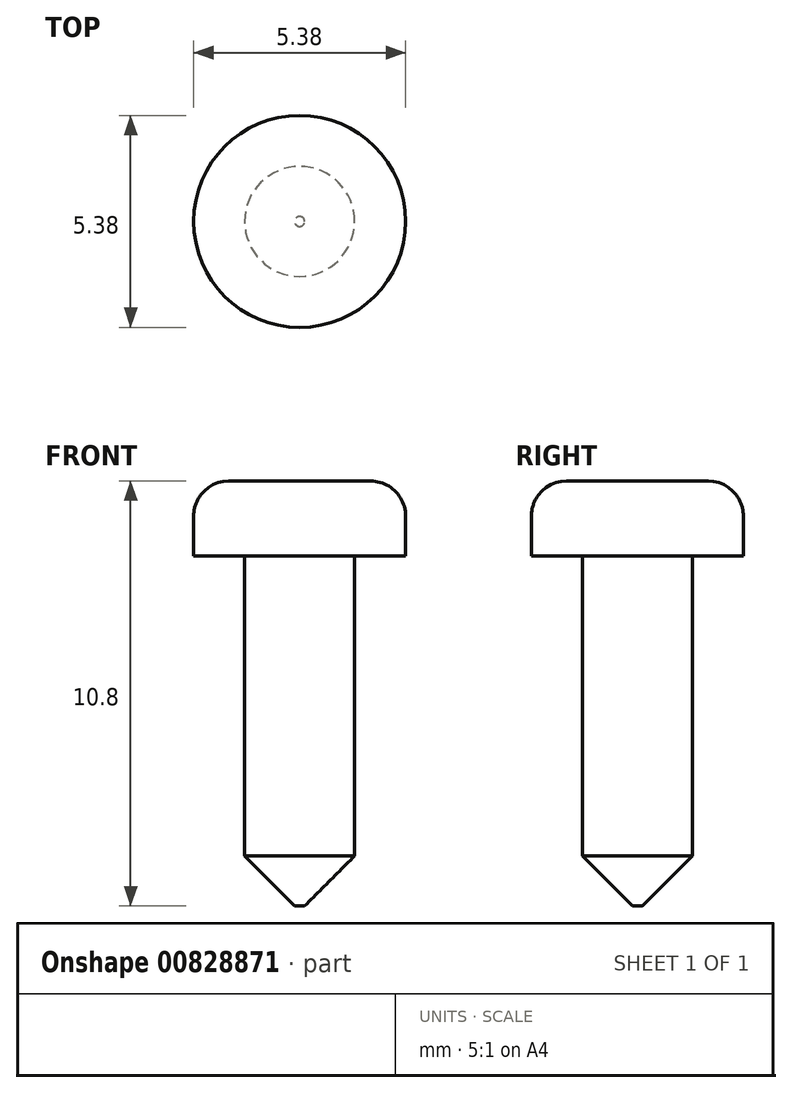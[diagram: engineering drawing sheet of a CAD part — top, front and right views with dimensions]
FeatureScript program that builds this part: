
annotation { "Feature Type Name" : "Feature", "Feature Type Description" : "" }
export const myFeature = defineFeature(function(context is Context, id is Id, definition is map)
    precondition{}
    {
        {
            var Q0;
            Q0=qCreatedBy(makeId("Top.planeOp"),FACE);
            var sketch = newSketch(context, id + "F0", { "sketchPlane" : qUnion([Q0])});
            skCircle(sketch, "E0", {"center": v(0, 0) * mm, "radius": 2.7 * mm});
            skSolve(sketch);
        }
        {
            var Q0;
            Q0 = qSketchRegion(id + "F0", true);
            extrude(context, id + "F1", {"entities" : qUnion([Q0]), "depth" : 1.9 * mm, "offsetDistance" : 25.4 * mm});
        }
        {
            var Q0;
            Q0=makeQuery(id+"F1.opExtrude","CAP_EDGE",EDGE,{"disambiguationData":[OSD([sQuery(id+"F0.wireOp",EDGE,"E0")])],"isStart":false});
            fillet(context, id + "F2", {"entities" : qUnion([Q0]), "radius" : 0.89 * mm, "tangentPropagation" : true, "allowEdgeOverflow" : false});
        }
        {
            var Q0;
            Q0=qCreatedBy(makeId("Top.planeOp"),FACE);
            var sketch = newSketch(context, id + "F3", { "sketchPlane" : qUnion([Q0])});
            skCircle(sketch, "E1", {"center": v(0, 0) * mm, "radius": 1.4 * mm});
            skSolve(sketch);
        }
        {
            var Q0;
            Q0 = qSketchRegion(id + "F3", true);
            extrude(context, id + "F4", {"entities" : qUnion([Q0]), "operationType" : NewBodyOperationType.ADD, "oppositeDirection" : true, "depth" : 8.9 * mm, "offsetDistance" : 25.4 * mm});
        }
        {
            var Q0;
            Q0=makeQuery(id+"F4.opExtrude","CAP_EDGE",EDGE,{"disambiguationData":[OSD([sQuery(id+"F3.wireOp",EDGE,"E1")])],"isStart":false});
            chamfer(context, id + "F5", {"entities" : qUnion([Q0]), "width" : 1.27 * mm, "tangentPropagation" : true});
        }
    });
